# Revit family: Block-Roseburg-OSB
name_source: partatom
category: Structural Framing
units: mm (PartAtom-declared; Revit-internal decimal feet)

## family parameters
Always export as geometry = No
Always vertical = Yes
Cut with Voids When Loaded = No
Material for Model Behavior = Other
Section Shape = Not Defined
Shared = No
Show family pre-cut in plan views = Yes
Structural Framing Length Roundoff = 0' - 0"
Work Plane-Based = Yes

## types (16) — shared parameters
Application Chart = https://www.roseburg.com
Assembly Code = B10
Building Codes = See PR-L289 & PR-L289C
Construction Details = https://www.arcat.com
Default Elevation = 4' - 0"
EWP Application Chart = https://www.arcat.com
Green Building-LEED = https://www.arcat.com
Installation Guide = https://www.arcat.com
Keynote = 06 40 00
Manufacturer = Roseburg
Material = OSB
Model = Squash Block
Product Data = https://www.arcat.com
Specification = https://www.arcat.com
Testing Data = See ESR1210
URL = https://www.roseburg.com

## per-type parameters (varying)
| type | Description | b | d |
| 3-1/2" Wide, 1-1/8" x 11-7/8" | 3-1/2" wide, 1-1/8” APA Rim Board or Rated Sturd-I-Floor 32 o.c. | 0' - 1 1/8" | 0' - 11 7/8" |
| 3-1/2" Wide, 1" x 9-1/2" | 3-1/2" wide, 1” APA Rim Board or Rated Sturd-I-Floor 32 o.c. | 0' - 1" | 0' - 9 1/2" |
| 3-1/2" Wide, 1-1/8" x 14" | 3-1/2" wide, 1-1/8” APA Rim Board or Rated Sturd-I-Floor 32 o.c. | 0' - 1 1/8" | 1' - 2" |
| 3-1/2" Wide, 1-1/8" x 9-1/2" | 3-1/2" wide, 1-1/8” APA Rim Board or Rated Sturd-I-Floor 32 o.c. | 0' - 1 1/8" | 0' - 9 1/2" |
| 3-1/2" Wide, 1" x 11-7/8" | 3-1/2" wide, 1” APA Rim Board or Rated Sturd-I-Floor 32 o.c. | 0' - 1" | 0' - 11 7/8" |
| 3-1/2" Wide, 1" x 14" | 3-1/2" wide, 1” APA Rim Board or Rated Sturd-I-Floor 32 o.c. | 0' - 1" | 1' - 2" |
| 3-1/2" Wide, 1" x 16" | 3-1/2" wide, 1” APA Rim Board or Rated Sturd-I-Floor 32 o.c. | 0' - 1" | 1' - 4" |
| 3-1/2" Wide, 1-1/8" x 16" | 3-1/2" wide, 1-1/8” APA Rim Board or Rated Sturd-I-Floor 32 o.c. | 0' - 1 1/8" | 1' - 4" |
| 5-1/2" Wide, 1" x 11-7/8" | 3-1/2" wide, 1” APA Rim Board or Rated Sturd-I-Floor 32 o.c. | 0' - 1" | 0' - 11 7/8" |
| 5-1/2" Wide, 1" x 14" | 3-1/2" wide, 1” APA Rim Board or Rated Sturd-I-Floor 32 o.c. | 0' - 1" | 1' - 2" |
| 5-1/2" Wide, 1" x 16" | 3-1/2" wide, 1” APA Rim Board or Rated Sturd-I-Floor 32 o.c. | 0' - 1" | 1' - 4" |
| 5-1/2" Wide, 1" x 9-1/2" | 3-1/2" wide, 1” APA Rim Board or Rated Sturd-I-Floor 32 o.c. | 0' - 1" | 0' - 9 1/2" |
| 5-1/2" Wide, 1-1/8" x 11-7/8" | 3-1/2" wide, 1-1/8” APA Rim Board or Rated Sturd-I-Floor 32 o.c. | 0' - 1 1/8" | 0' - 11 7/8" |
| 5-1/2" Wide, 1-1/8" x 14" | 3-1/2" wide, 1-1/8” APA Rim Board or Rated Sturd-I-Floor 32 o.c. | 0' - 1 1/8" | 1' - 2" |
| 5-1/2" Wide, 1-1/8" x 16" | 3-1/2" wide, 1-1/8” APA Rim Board or Rated Sturd-I-Floor 32 o.c. | 0' - 1 1/8" | 1' - 4" |
| 5-1/2" Wide, 1-1/8" x 9-1/2" | 3-1/2" wide, 1-1/8” APA Rim Board or Rated Sturd-I-Floor 32 o.c. | 0' - 1 1/8" | 0' - 9 1/2" |

## geometry (parser evidence)
native form markers: Sweep x3
no freeform markers — native parametric forms only
